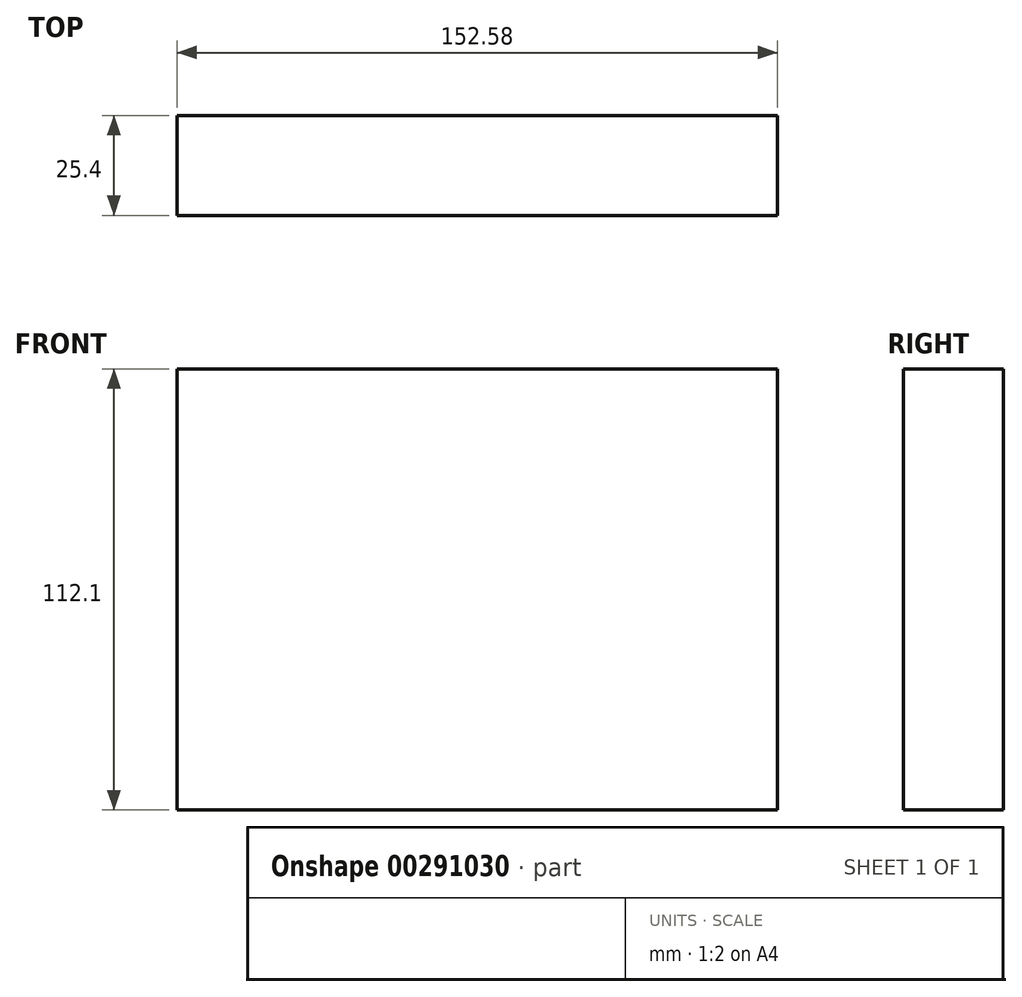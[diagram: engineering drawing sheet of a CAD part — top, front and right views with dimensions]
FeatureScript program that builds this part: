
annotation { "Feature Type Name" : "Feature", "Feature Type Description" : "" }
export const myFeature = defineFeature(function(context is Context, id is Id, definition is map)
    precondition{}
    {
        {
            var Q0;
            Q0=qCreatedBy(makeId("Front.planeOp"),FACE);
            var sketch = newSketch(context, id + "F0", { "sketchPlane" : qUnion([Q0])});
            skLineSegment(sketch, "E0.bottom", {"start": v(-76.34, -56.05) * mm, "end": v(76.24, -56.05) * mm});
            skLineSegment(sketch, "E0.top", {"start": v(-76.34, 56.05) * mm, "end": v(76.24, 56.05) * mm});
            skLineSegment(sketch, "E0.left", {"start": v(-76.34, -56.05) * mm, "end": v(-76.34, 56.05) * mm});
            skLineSegment(sketch, "E0.right", {"start": v(76.24, -56.05) * mm, "end": v(76.24, 56.05) * mm});
            skSolve(sketch);
        }
        {
            var Q0;
            Q0 = qSketchRegion(id + "F0", true);
            extrude(context, id + "F1", {"entities" : qUnion([Q0]), "endBound" : BoundingType.SYMMETRIC, "oppositeDirection" : true, "depth" : 25.4 * mm});
        }
    });
